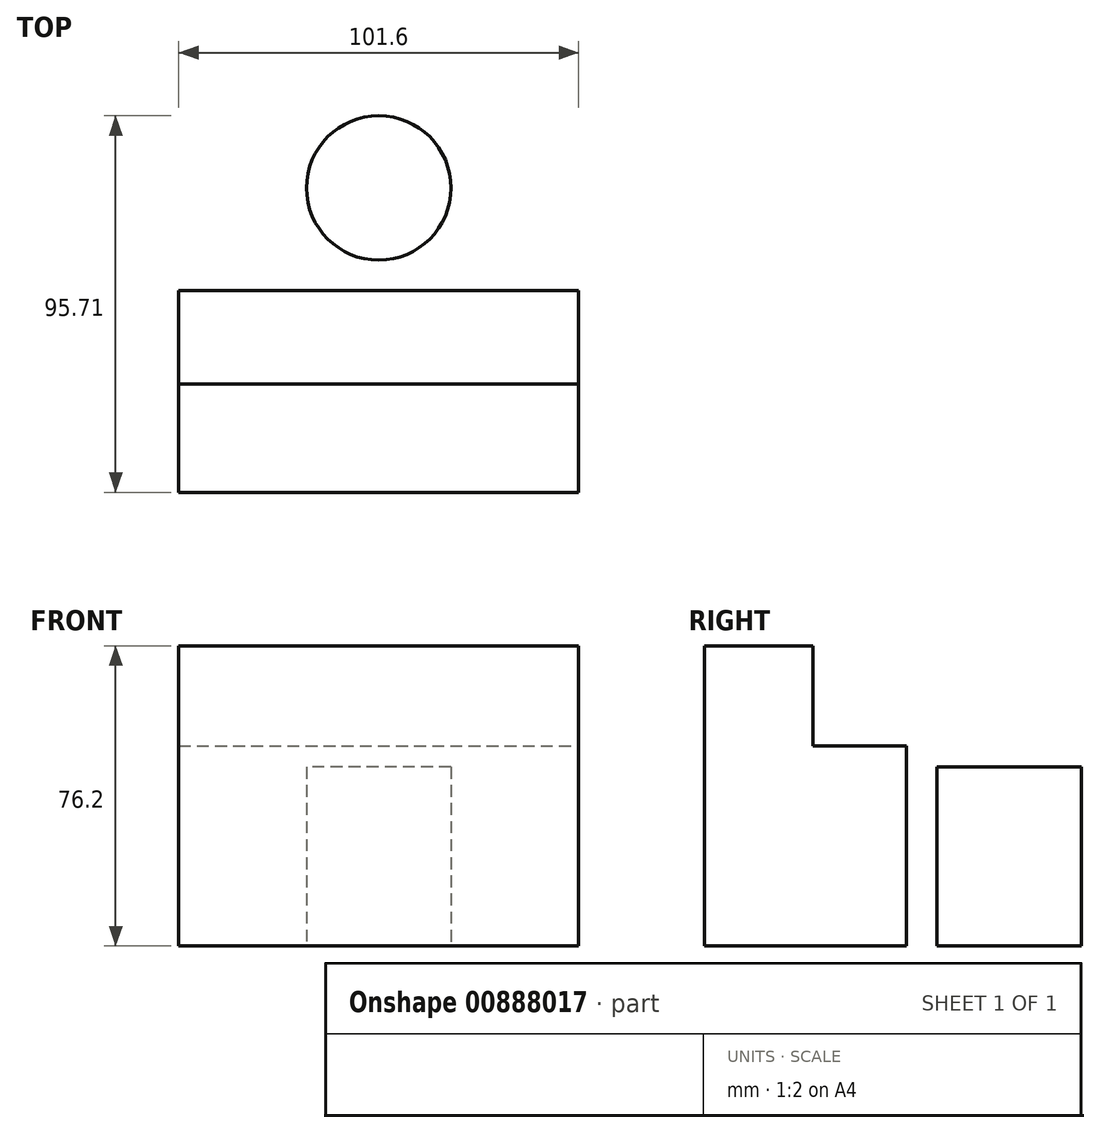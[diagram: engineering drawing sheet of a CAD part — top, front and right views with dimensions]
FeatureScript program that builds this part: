
annotation { "Feature Type Name" : "Feature", "Feature Type Description" : "" }
export const myFeature = defineFeature(function(context is Context, id is Id, definition is map)
    precondition{}
    {
        {
            var Q0;
            Q0=qCreatedBy(makeId("Top.planeOp"),FACE);
            var sketch = newSketch(context, id + "F0", { "sketchPlane" : qUnion([Q0])});
            skLineSegment(sketch, "E0.bottom", {"start": v(-50.8, -27.53) * mm, "end": v(50.8, -27.53) * mm});
            skLineSegment(sketch, "E0.top", {"start": v(-50.8, 23.77) * mm, "end": v(50.8, 23.77) * mm});
            skLineSegment(sketch, "E0.left", {"start": v(-50.8, -27.53) * mm, "end": v(-50.8, 23.77) * mm});
            skLineSegment(sketch, "E0.right", {"start": v(50.8, -27.53) * mm, "end": v(50.8, 23.77) * mm});
            skSolve(sketch);
        }
        {
            var Q0;
            Q0=makeQuery(id+"F0.imprint","IMPRINT",FACE,{"disambiguationData":[TD([[makeQuery(id+"F0.imprint","IMPRINT",EDGE,{"derivedFrom":sQuery(id+"F0.wireOp",EDGE,"E0.bottom")}),1.0]])]});
            extrude(context, id + "F1", {"entities" : qUnion([Q0]), "depth" : 76.2 * mm, "offsetDistance" : 25.4 * mm});
        }
        {
            var Q0;
            Q0=makeQuery(id+"F1.opExtrude","CAP_FACE",FACE,{"disambiguationData":[OSD([sQuery(id+"F0.wireOp",EDGE,"E0.bottom"),sQuery(id+"F0.wireOp",EDGE,"E0.top"),sQuery(id+"F0.wireOp",EDGE,"E0.left"),sQuery(id+"F0.wireOp",EDGE,"E0.right")])],"isStart":false});
            var sketch = newSketch(context, id + "F2", { "sketchPlane" : qUnion([Q0])});
            skLineSegment(sketch, "E1.bottom", {"start": v(-50.8, 23.77) * mm, "end": v(50.8, 23.77) * mm});
            skLineSegment(sketch, "E1.top", {"start": v(-50.8, 0) * mm, "end": v(50.8, 0) * mm});
            skLineSegment(sketch, "E1.left", {"start": v(-50.8, 23.77) * mm, "end": v(-50.8, 0) * mm});
            skLineSegment(sketch, "E1.right", {"start": v(50.8, 23.77) * mm, "end": v(50.8, 0) * mm});
            skSolve(sketch);
        }
        {
            var Q0;
            Q0=makeQuery(id+"F2.imprint","IMPRINT",FACE,{"disambiguationData":[TD([[makeQuery(id+"F2.imprint","IMPRINT",EDGE,{"derivedFrom":sQuery(id+"F2.wireOp",EDGE,"E1.bottom")}),-1.0]])]});
            extrude(context, id + "F3", {"entities" : qUnion([Q0]), "operationType" : NewBodyOperationType.REMOVE, "oppositeDirection" : true, "depth" : 25.4 * mm, "offsetDistance" : 25.4 * mm});
        }
        {
            var Q0;
            Q0=qCreatedBy(makeId("Top.planeOp"),FACE);
            var sketch = newSketch(context, id + "F4", { "sketchPlane" : qUnion([Q0])});
            skCircle(sketch, "E2", {"center": v(0, 49.83) * mm, "radius": 18.35 * mm});
            skSolve(sketch);
        }
        {
            var Q0;
            Q0=makeQuery(id+"F4.imprint","IMPRINT",FACE,{"disambiguationData":[TD([[makeQuery(id+"F4.imprint","IMPRINT",EDGE,{"derivedFrom":sQuery(id+"F4.wireOp",EDGE,"E2")}),1.0]])]});
            extrude(context, id + "F5", {"entities" : qUnion([Q0]), "depth" : 45.47 * mm, "offsetDistance" : 25.4 * mm});
        }
    });
